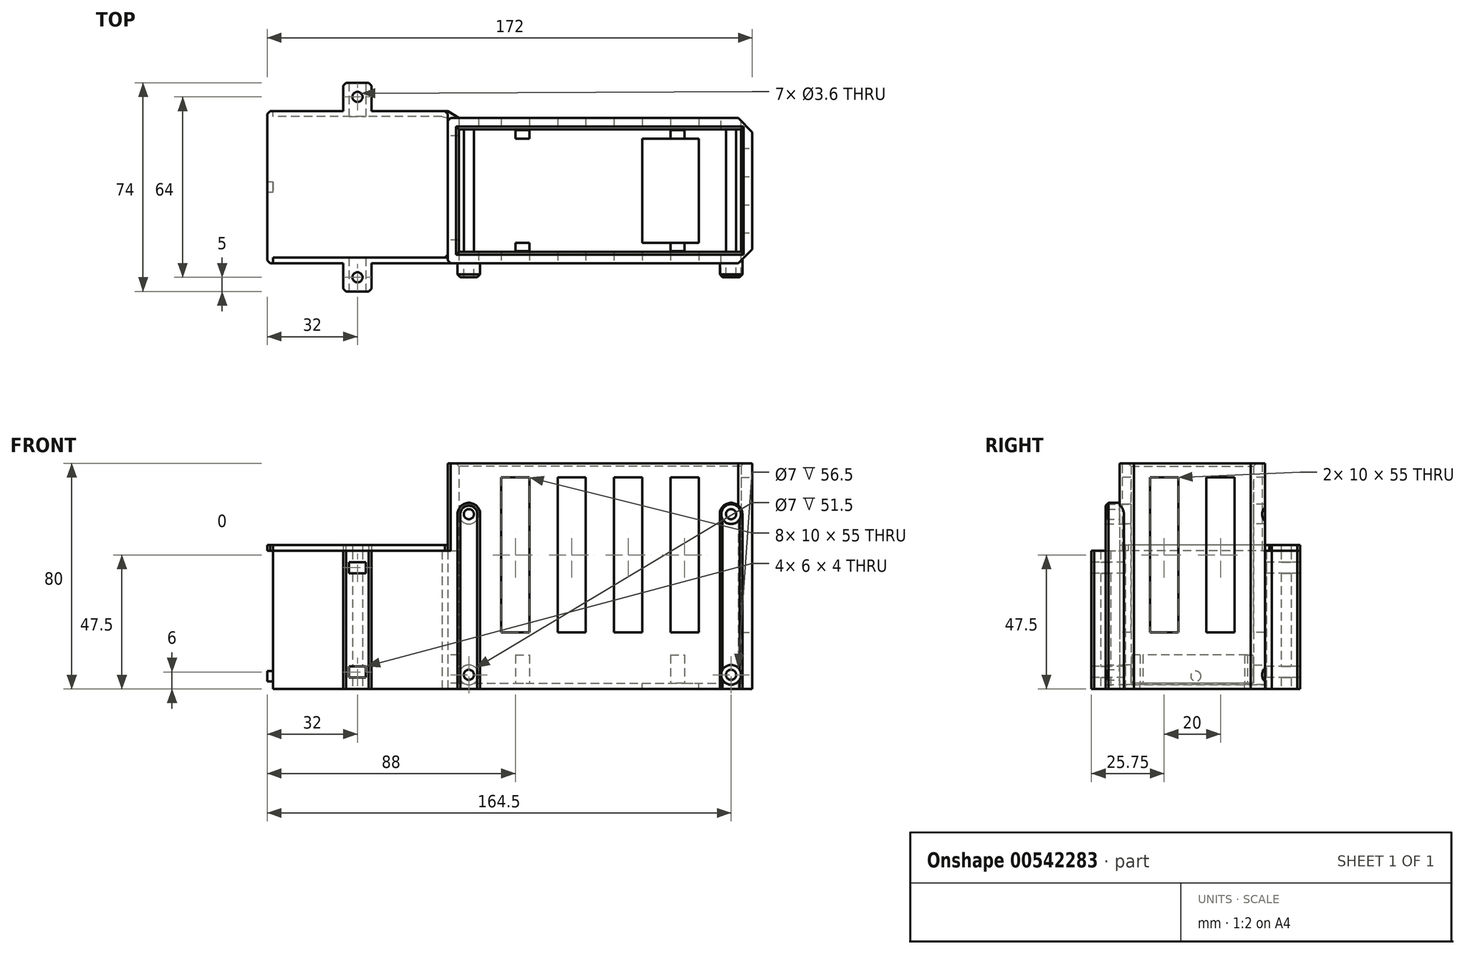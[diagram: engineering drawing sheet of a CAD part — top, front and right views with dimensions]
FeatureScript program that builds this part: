
annotation { "Feature Type Name" : "Feature", "Feature Type Description" : "" }
export const myFeature = defineFeature(function(context is Context, id is Id, definition is map)
    precondition{}
    {
        {
            var Q0;
            Q0=qCreatedBy(makeId("Top.planeOp"),FACE);
            var sketch = newSketch(context, id + "F0", { "sketchPlane" : qUnion([Q0])});
            skLineSegment(sketch, "E0.bottom", {"start": v(-50, 21.75) * mm, "end": v(50, 21.75) * mm});
            skLineSegment(sketch, "E0.top", {"start": v(-50, -21.75) * mm, "end": v(50, -21.75) * mm});
            skLineSegment(sketch, "E0.left", {"start": v(-50, 21.75) * mm, "end": v(-50, -21.75) * mm});
            skLineSegment(sketch, "E0.right", {"start": v(50, 21.75) * mm, "end": v(50, -21.75) * mm});
            skPoint(sketch, "E0.middle", {"position": v(0, 0) * mm});
            skLineSegment(sketch, "E1.0", {"start": v(-54, 25.75) * mm, "end": v(54, 25.75) * mm});
            skLineSegment(sketch, "E1.1", {"start": v(-54, 25.75) * mm, "end": v(-54, -25.75) * mm});
            skLineSegment(sketch, "E1.2", {"start": v(-54, -25.75) * mm, "end": v(54, -25.75) * mm});
            skLineSegment(sketch, "E1.3", {"start": v(54, 25.75) * mm, "end": v(54, -25.75) * mm});
            skLineSegment(sketch, "E2.bottom", {"start": v(-54, -25.75) * mm, "end": v(-118, -25.75) * mm});
            skLineSegment(sketch, "E2.top", {"start": v(-54, 28.25) * mm, "end": v(-118, 28.25) * mm});
            skLineSegment(sketch, "E2.left", {"start": v(-54, -25.75) * mm, "end": v(-54, 25.75) * mm});
            skLineSegment(sketch, "E2.right", {"start": v(-118, -25.75) * mm, "end": v(-118, 28.25) * mm});
            skLineSegment(sketch, "E3.1", {"start": v(-56, -23.75) * mm, "end": v(-116, -23.75) * mm});
            skLineSegment(sketch, "E3.2", {"start": v(-116, -23.75) * mm, "end": v(-116, 26.25) * mm});
            skLineSegment(sketch, "E3.3", {"start": v(-56, 26.25) * mm, "end": v(-116, 26.25) * mm});
            skLineSegment(sketch, "E4", {"start": v(-54, 28.25) * mm, "end": v(-49.99, 25.75) * mm});
            skLineSegment(sketch, "E5", {"start": v(-86, 28.25) * mm, "end": v(-86, 33.25) * mm, "construction": true});
            skLineSegment(sketch, "E6", {"start": v(-116, 1.25) * mm, "end": v(-77.24, 1.25) * mm, "construction": true});
            skLineSegment(sketch, "E7.bottom", {"start": v(-91, 38.25) * mm, "end": v(-81, 38.25) * mm});
            skLineSegment(sketch, "E7.top", {"start": v(-91, 28.25) * mm, "end": v(-81, 28.25) * mm});
            skLineSegment(sketch, "E7.left", {"start": v(-91, 38.25) * mm, "end": v(-91, 28.25) * mm});
            skLineSegment(sketch, "E7.right", {"start": v(-81, 38.25) * mm, "end": v(-81, 28.25) * mm});
            skPoint(sketch, "E7.middle", {"position": v(-86, 33.25) * mm});
            skCircle(sketch, "E8", {"center": v(-86, 33.25) * mm, "radius": 1.8 * mm});
            skLineSegment(sketch, "E9.MirrorCS", {"start": v(-91, -35.75) * mm, "end": v(-91, -25.75) * mm});
            skLineSegment(sketch, "E10.MirrorCS", {"start": v(-91, -35.75) * mm, "end": v(-81, -35.75) * mm});
            skLineSegment(sketch, "E11.MirrorCS", {"start": v(-81, -35.75) * mm, "end": v(-81, -25.75) * mm});
            skCircle(sketch, "E12.MirrorC", {"center": v(-86, -30.75) * mm, "radius": 1.8 * mm});
            skLineSegment(sketch, "E13", {"start": v(-56, 26.25) * mm, "end": v(-54, 25.75) * mm});
            skLineSegment(sketch, "E14", {"start": v(-56, -23.75) * mm, "end": v(-54, -23.75) * mm});
            skSolve(sketch);
        }
        {
            var Q0;
            Q0=makeQuery(id+"F0.imprint","IMPRINT",FACE,{"disambiguationData":[TD([[makeQuery(id+"F0.imprint","IMPRINT",EDGE,{"derivedFrom":sQuery(id+"F0.wireOp",EDGE,"E0.bottom")}),1.0]])]});
            extrude(context, id + "F1", {"entities" : qUnion([Q0]), "depth" : 80 * mm, "offsetDistance" : 25 * mm});
        }
        {
            var Q0;
            Q0=makeQuery(id+"F0.imprint","IMPRINT",FACE,{"disambiguationData":[TD([[makeQuery(id+"F0.imprint","IMPRINT",EDGE,{"derivedFrom":sQuery(id+"F0.wireOp",EDGE,"E0.bottom")}),-1.0]])]});
            extrude(context, id + "F2", {"entities" : qUnion([Q0]), "operationType" : NewBodyOperationType.ADD, "depth" : 2 * mm, "offsetDistance" : 25 * mm});
        }
        {
            var Q0;
            Q0=makeQuery(id+"F1.opExtrude","SWEPT_FACE",FACE,{"disambiguationData":[OSD([sQuery(id+"F0.wireOp",EDGE,"E1.2")])]});
            var sketch = newSketch(context, id + "F3", { "sketchPlane" : qUnion([Q0])});
            skLineSegment(sketch, "E15.bottom", {"start": v(-46.5, 62) * mm, "end": v(46.5, 62) * mm, "construction": true});
            skLineSegment(sketch, "E15.top", {"start": v(-46.5, 5) * mm, "end": v(46.5, 5) * mm, "construction": true});
            skLineSegment(sketch, "E15.left", {"start": v(-46.5, 62) * mm, "end": v(-46.5, 5) * mm, "construction": true});
            skLineSegment(sketch, "E15.right", {"start": v(46.5, 62) * mm, "end": v(46.5, 5) * mm, "construction": true});
            skArc(sketch, "E16", {"start": v(-42.5, 62) * mm, "mid": v(-46.5, 66) * mm, "end": v(-50.5, 62) * mm});
            skLineSegment(sketch, "E17", {"start": v(-50.5, 62) * mm, "end": v(-50.5, 0) * mm});
            skLineSegment(sketch, "E18", {"start": v(-42.5, 62) * mm, "end": v(-42.5, 0) * mm});
            skCircle(sketch, "E19", {"center": v(-46.5, 62) * mm, "radius": 1.8 * mm});
            skCircle(sketch, "E20", {"center": v(-46.5, 5) * mm, "radius": 1.8 * mm});
            skLineSegment(sketch, "E21", {"start": v(0, 0) * mm, "end": v(0, 80) * mm, "construction": true});
            skCircle(sketch, "E22.MirrorC", {"center": v(46.5, 62) * mm, "radius": 1.8 * mm});
            skLineSegment(sketch, "E23.MirrorCS", {"start": v(42.5, 62) * mm, "end": v(42.5, 0) * mm});
            skArc(sketch, "E24.MirrorCS", {"start": v(42.5, 62) * mm, "mid": v(46.5, 66) * mm, "end": v(50.5, 62) * mm});
            skLineSegment(sketch, "E25.MirrorCS", {"start": v(50.5, 62) * mm, "end": v(50.5, 0) * mm});
            skCircle(sketch, "E26.MirrorC", {"center": v(46.5, 5) * mm, "radius": 1.8 * mm});
            skCircle(sketch, "E27", {"center": v(-46.5, 62) * mm, "radius": 3.5 * mm});
            skCircle(sketch, "E28", {"center": v(-46.5, 5) * mm, "radius": 3.5 * mm});
            skCircle(sketch, "E29.MirrorC", {"center": v(46.5, 62) * mm, "radius": 3.5 * mm});
            skCircle(sketch, "E30.MirrorC", {"center": v(46.5, 5) * mm, "radius": 3.5 * mm});
            skSolve(sketch);
        }
        {
            var Q0;
            Q0=makeQuery(id+"F3.imprint","IMPRINT",FACE,{"disambiguationData":[TD([[makeQuery(id+"F3.imprint","IMPRINT",EDGE,{"derivedFrom":sQuery(id+"F3.wireOp",EDGE,"E22.MirrorC")}),1.0]])]});
            var Q1;
            Q1=makeQuery(id+"F3.imprint","IMPRINT",FACE,{"disambiguationData":[TD([[makeQuery(id+"F3.imprint","IMPRINT",EDGE,{"derivedFrom":sQuery(id+"F3.wireOp",EDGE,"E16")}),1.0]])]});
            var Q2;
            Q2=makeQuery(id+"F3.imprint","IMPRINT",FACE,{"disambiguationData":[TD([[makeQuery(id+"F3.imprint","IMPRINT",EDGE,{"derivedFrom":sQuery(id+"F3.wireOp",EDGE,"E19")}),-1.0]])]});
            var Q3;
            Q3=makeQuery(id+"F3.imprint","IMPRINT",FACE,{"disambiguationData":[TD([[makeQuery(id+"F3.imprint","IMPRINT",EDGE,{"derivedFrom":sQuery(id+"F3.wireOp",EDGE,"E20")}),-1.0]])]});
            var Q4;
            {var subQ1=sQuery(id+"F3.wireOp",EDGE,"E23.MirrorCS");Q4=makeQuery(id+"F3.imprint","IMPRINT",FACE,{"disambiguationData":[TD([[makeQuery(id+"F3.imprint","IMPRINT",EDGE,{"derivedFrom":subQ1}),1.0]])]});}
            var Q5;
            Q5=makeQuery(id+"F3.imprint","IMPRINT",FACE,{"disambiguationData":[TD([[makeQuery(id+"F3.imprint","IMPRINT",EDGE,{"derivedFrom":sQuery(id+"F3.wireOp",EDGE,"E26.MirrorC")}),1.0]])]});
            extrude(context, id + "F4", {"entities" : qUnion([Q0, Q1, Q2, Q3, Q4, Q5]), "operationType" : NewBodyOperationType.ADD, "depth" : 5 * mm, "offsetDistance" : 25 * mm});
        }
        {
            var Q0;
            Q0=makeQuery(id+"F3.imprint","IMPRINT",FACE,{"disambiguationData":[TD([[makeQuery(id+"F3.imprint","IMPRINT",EDGE,{"derivedFrom":sQuery(id+"F3.wireOp",EDGE,"E20")}),-1.0]])]});
            var Q1;
            Q1=makeQuery(id+"F3.imprint","IMPRINT",FACE,{"disambiguationData":[TD([[makeQuery(id+"F3.imprint","IMPRINT",EDGE,{"derivedFrom":sQuery(id+"F3.wireOp",EDGE,"E26.MirrorC")}),1.0]])]});
            var Q2;
            Q2=makeQuery(id+"F3.imprint","IMPRINT",FACE,{"disambiguationData":[TD([[makeQuery(id+"F3.imprint","IMPRINT",EDGE,{"derivedFrom":sQuery(id+"F3.wireOp",EDGE,"E22.MirrorC")}),1.0]])]});
            var Q3;
            Q3=makeQuery(id+"F3.imprint","IMPRINT",FACE,{"disambiguationData":[TD([[makeQuery(id+"F3.imprint","IMPRINT",EDGE,{"derivedFrom":sQuery(id+"F3.wireOp",EDGE,"E22.MirrorC")}),-1.0]])]});
            var Q4;
            Q4=makeQuery(id+"F3.imprint","IMPRINT",FACE,{"disambiguationData":[TD([[makeQuery(id+"F3.imprint","IMPRINT",EDGE,{"derivedFrom":sQuery(id+"F3.wireOp",EDGE,"E26.MirrorC")}),-1.0]])]});
            var Q5;
            Q5=makeQuery(id+"F3.imprint","IMPRINT",FACE,{"disambiguationData":[TD([[makeQuery(id+"F3.imprint","IMPRINT",EDGE,{"derivedFrom":sQuery(id+"F3.wireOp",EDGE,"E20")}),1.0]])]});
            var Q6;
            Q6=makeQuery(id+"F3.imprint","IMPRINT",FACE,{"disambiguationData":[TD([[makeQuery(id+"F3.imprint","IMPRINT",EDGE,{"derivedFrom":sQuery(id+"F3.wireOp",EDGE,"E19")}),-1.0]])]});
            var Q7;
            Q7=makeQuery(id+"F3.imprint","IMPRINT",FACE,{"disambiguationData":[TD([[makeQuery(id+"F3.imprint","IMPRINT",EDGE,{"derivedFrom":sQuery(id+"F3.wireOp",EDGE,"E19")}),1.0]])]});
            extrude(context, id + "F5", {"entities" : qUnion([Q0, Q1, Q2, Q3, Q4, Q5, Q6, Q7]), "operationType" : NewBodyOperationType.REMOVE, "oppositeDirection" : true, "depth" : 58 * mm, "offsetDistance" : 25 * mm});
        }
        {
            var Q0;
            {var subQ0=sQuery(id+"F0.wireOp",EDGE,"E0.bottom");var subQ1=makeQuery(id+"F1.opExtrude","SWEPT_FACE",FACE,{"disambiguationData":[OSD([subQ0])]});var subQ2=makeQuery(id+"F5.opExtrude","SWEPT_FACE",FACE,{"disambiguationData":[OSD([sQuery(id+"F3.wireOp",EDGE,"E28")])]});var subQ3=sQuery(id+"F0.wireOp",EDGE,"E0.top");var subQ4=makeQuery(id+"F1.opExtrude","SWEPT_FACE",FACE,{"disambiguationData":[OSD([subQ3])]});var subQ5=makeQuery(id+"F5.opExtrude","SWEPT_FACE",FACE,{"disambiguationData":[OSD([sQuery(id+"F3.wireOp",EDGE,"E30.MirrorC")])]});var subQ6=sQuery(id+"F0.wireOp",EDGE,"E0.right");var subQ7=sQuery(id+"F0.wireOp",EDGE,"E0.left");var subQ8=makeQuery(id+"F2.opExtrude","CAP_FACE",FACE,{"disambiguationData":[OSD([subQ0,subQ3,subQ7,subQ6])],"isStart":false});Q0=qUnion([makeQuery(id+"F5.boolean.opBoolean","SPLIT",FACE,{"disambiguationData":[TD([subQ1,subQ4,makeQuery(id+"F1.opExtrude","SWEPT_FACE",FACE,{"disambiguationData":[OSD([subQ7])]}),subQ2])],"derivedFrom":subQ8}),makeQuery(id+"F5.boolean.opBoolean","SPLIT",FACE,{"disambiguationData":[TD([subQ1,subQ4,makeQuery(id+"F1.opExtrude","SWEPT_FACE",FACE,{"disambiguationData":[OSD([subQ6])]}),subQ5])],"derivedFrom":subQ8}),makeQuery(id+"F5.boolean.opBoolean","SPLIT",FACE,{"disambiguationData":[TD([subQ1,subQ4,subQ2,subQ5])],"derivedFrom":subQ8})]);}
            var sketch = newSketch(context, id + "F6", { "sketchPlane" : qUnion([Q0])});
            skPoint(sketch, "E31.middle", {"position": v(0, 0) * mm});
            skLineSegment(sketch, "E32.bottom", {"start": v(-30, 18.5) * mm, "end": v(30, 18.5) * mm, "construction": true});
            skLineSegment(sketch, "E32.top", {"start": v(-30, -18.5) * mm, "end": v(30, -18.5) * mm, "construction": true});
            skLineSegment(sketch, "E32.left", {"start": v(-30, 18.5) * mm, "end": v(-30, -18.5) * mm, "construction": true});
            skLineSegment(sketch, "E32.right", {"start": v(30, 18.5) * mm, "end": v(30, -18.5) * mm, "construction": true});
            skLineSegment(sketch, "E33.bottom", {"start": v(-30, 18.5) * mm, "end": v(-25, 18.5) * mm});
            skLineSegment(sketch, "E33.top", {"start": v(-30, 21.5) * mm, "end": v(-25, 21.5) * mm});
            skLineSegment(sketch, "E33.left", {"start": v(-30, 18.5) * mm, "end": v(-30, 21.5) * mm});
            skLineSegment(sketch, "E33.right", {"start": v(-25, 18.5) * mm, "end": v(-25, 21.5) * mm});
            skLineSegment(sketch, "E34", {"start": v(0, 0) * mm, "end": v(0, 7.27) * mm, "construction": true});
            skLineSegment(sketch, "E35", {"start": v(0, 0) * mm, "end": v(-7.02, 0) * mm, "construction": true});
            skLineSegment(sketch, "E36.MirrorCS", {"start": v(-25, -18.5) * mm, "end": v(-25, -21.5) * mm});
            skLineSegment(sketch, "E37.MirrorCS", {"start": v(-30, -18.5) * mm, "end": v(-30, -21.5) * mm});
            skLineSegment(sketch, "E38.MirrorCS", {"start": v(-30, -21.5) * mm, "end": v(-25, -21.5) * mm});
            skLineSegment(sketch, "E39.MirrorCS", {"start": v(25, 18.5) * mm, "end": v(25, 21.5) * mm});
            skLineSegment(sketch, "E40.MirrorCS", {"start": v(30, 18.5) * mm, "end": v(30, 21.5) * mm});
            skLineSegment(sketch, "E41.MirrorCS", {"start": v(25, -18.5) * mm, "end": v(25, -21.5) * mm});
            skLineSegment(sketch, "E42.MirrorCS", {"start": v(30, -18.5) * mm, "end": v(30, -21.5) * mm});
            skLineSegment(sketch, "E43.MirrorCS", {"start": v(30, 21.5) * mm, "end": v(25, 21.5) * mm});
            skLineSegment(sketch, "E44.MirrorCS", {"start": v(30, -21.5) * mm, "end": v(25, -21.5) * mm});
            skLineSegment(sketch, "E45", {"start": v(25, 18.5) * mm, "end": v(30, 18.5) * mm});
            skLineSegment(sketch, "E46", {"start": v(-30, -18.5) * mm, "end": v(-25, -18.5) * mm});
            skLineSegment(sketch, "E47", {"start": v(25, -18.5) * mm, "end": v(30, -18.5) * mm});
            skLineSegment(sketch, "E48", {"start": v(0, 0) * mm, "end": v(25, 0) * mm, "construction": true});
            skLineSegment(sketch, "E49.bottom", {"start": v(15, 18.5) * mm, "end": v(35, 18.5) * mm});
            skLineSegment(sketch, "E49.top", {"start": v(15, -18.5) * mm, "end": v(35, -18.5) * mm});
            skLineSegment(sketch, "E49.left", {"start": v(15, 18.5) * mm, "end": v(15, -18.5) * mm});
            skLineSegment(sketch, "E49.right", {"start": v(35, 18.5) * mm, "end": v(35, -18.5) * mm});
            skPoint(sketch, "E49.middle", {"position": v(25, 0) * mm});
            skSolve(sketch);
        }
        {
            var Q0;
            {var subQ4=sQuery(id+"F0.wireOp",EDGE,"E2.right");Q0=makeQuery(id+"F0.imprint","IMPRINT",FACE,{"disambiguationData":[TD([[makeQuery(id+"F0.imprint","IMPRINT",EDGE,{"derivedFrom":subQ4}),-1.0]])]});}
            var Q1;
            Q1=makeQuery(id+"F0.imprint","IMPRINT",FACE,{"disambiguationData":[TD([[makeQuery(id+"F0.imprint","IMPRINT",EDGE,{"derivedFrom":sQuery(id+"F0.wireOp",EDGE,"E7.bottom")}),-1.0]])]});
            var Q2;
            {var subQ0=sQuery(id+"F0.wireOp",EDGE,"E9.MirrorCS");Q2=makeQuery(id+"F0.imprint","IMPRINT",FACE,{"disambiguationData":[TD([[makeQuery(id+"F0.imprint","IMPRINT",EDGE,{"derivedFrom":subQ0}),-1.0]])]});}
            extrude(context, id + "F7", {"entities" : qUnion([Q0, Q1, Q2]), "operationType" : NewBodyOperationType.ADD, "depth" : 49 * mm, "offsetDistance" : 25 * mm});
        }
        {
            var Q0;
            Q0=makeQuery(id+"F7.opExtrude","SWEPT_FACE",FACE,{"disambiguationData":[OSD([sQuery(id+"F0.wireOp",EDGE,"E2.right")])]});
            var sketch = newSketch(context, id + "F8", { "sketchPlane" : qUnion([Q0])});
            skLineSegment(sketch, "E50.bottom", {"start": v(-26.25, 39.5) * mm, "end": v(23.75, 39.5) * mm});
            skLineSegment(sketch, "E50.top", {"start": v(-26.25, 9.5) * mm, "end": v(23.75, 9.5) * mm});
            skLineSegment(sketch, "E50.left", {"start": v(-26.25, 39.5) * mm, "end": v(-26.25, 9.5) * mm});
            skLineSegment(sketch, "E50.right", {"start": v(23.75, 39.5) * mm, "end": v(23.75, 9.5) * mm});
            skPoint(sketch, "E50.middle", {"position": v(-1.25, 24.5) * mm});
            skPoint(sketch, "E50.middle.positionSnap0", {"position": v(25.75, 24.5) * mm});
            skPoint(sketch, "E50.middle.positionSnap1", {"position": v(-1.25, 0) * mm});
            skPoint(sketch, "E50.centerSnap0", {"position": v(25.75, 24.5) * mm});
            skPoint(sketch, "E50.centerSnap1", {"position": v(-1.25, 0) * mm});
            skLineSegment(sketch, "E51", {"start": v(-1.25, 24.5) * mm, "end": v(-1.25, 44.5) * mm, "construction": true});
            skLineSegment(sketch, "E52", {"start": v(-1.25, 24.5) * mm, "end": v(-7.71, 24.5) * mm, "construction": true});
            skCircle(sketch, "E53", {"center": v(-1.25, 44.5) * mm, "radius": 1.8 * mm});
            skCircle(sketch, "E54.MirrorC", {"center": v(-1.25, 4.5) * mm, "radius": 1.8 * mm});
            skSolve(sketch);
        }
        {
            var Q0;
            Q0=makeQuery(id+"F8.imprint","IMPRINT",FACE,{"disambiguationData":[TD([[makeQuery(id+"F8.imprint","IMPRINT",EDGE,{"derivedFrom":sQuery(id+"F8.wireOp",EDGE,"E50.bottom")}),-1.0]])]});
            var Q1;
            Q1=makeQuery(id+"F8.imprint","IMPRINT",FACE,{"disambiguationData":[TD([[makeQuery(id+"F8.imprint","IMPRINT",EDGE,{"derivedFrom":sQuery(id+"F8.wireOp",EDGE,"E54.MirrorC")}),-1.0]])]});
            var Q2;
            Q2=makeQuery(id+"F8.imprint","IMPRINT",FACE,{"disambiguationData":[TD([[makeQuery(id+"F8.imprint","IMPRINT",EDGE,{"derivedFrom":sQuery(id+"F8.wireOp",EDGE,"E53")}),1.0]])]});
            extrude(context, id + "F9", {"entities" : qUnion([Q0, Q1, Q2]), "operationType" : NewBodyOperationType.REMOVE, "oppositeDirection" : true, "depth" : 2 * mm, "offsetDistance" : 25 * mm});
        }
        {
            var Q0;
            Q0=makeQuery(id+"F6.imprint","IMPRINT",FACE,{"disambiguationData":[TD([[makeQuery(id+"F6.imprint","IMPRINT",EDGE,{"derivedFrom":sQuery(id+"F6.wireOp",EDGE,"E33.bottom")}),1.0]])]});
            var Q1;
            {var subQ0=sQuery(id+"F6.wireOp",EDGE,"E36.MirrorCS");Q1=makeQuery(id+"F6.imprint","IMPRINT",FACE,{"disambiguationData":[TD([[makeQuery(id+"F6.imprint","IMPRINT",EDGE,{"derivedFrom":subQ0}),-1.0]])]});}
            var Q2;
            {var subQ0=sQuery(id+"F6.wireOp",EDGE,"E41.MirrorCS");Q2=makeQuery(id+"F6.imprint","IMPRINT",FACE,{"disambiguationData":[TD([[makeQuery(id+"F6.imprint","IMPRINT",EDGE,{"derivedFrom":subQ0}),1.0]])]});}
            var Q3;
            {var subQ0=sQuery(id+"F6.wireOp",EDGE,"E39.MirrorCS");Q3=makeQuery(id+"F6.imprint","IMPRINT",FACE,{"disambiguationData":[TD([[makeQuery(id+"F6.imprint","IMPRINT",EDGE,{"derivedFrom":subQ0}),-1.0]])]});}
            extrude(context, id + "F10", {"entities" : qUnion([Q0, Q1, Q2, Q3]), "operationType" : NewBodyOperationType.ADD, "depth" : 10 * mm, "offsetDistance" : 25 * mm});
        }
        {
            var Q0;
            Q0=makeQuery(id+"F1.opExtrude","SWEPT_FACE",FACE,{"disambiguationData":[OSD([sQuery(id+"F0.wireOp",EDGE,"E1.1")])]});
            var sketch = newSketch(context, id + "F11", { "sketchPlane" : qUnion([Q0])});
            skLineSegment(sketch, "E55", {"start": v(-1, 0) * mm, "end": v(-1, 7) * mm, "construction": true});
            skLineSegment(sketch, "E56.bottom", {"start": v(-19.5, 12) * mm, "end": v(17.5, 12) * mm});
            skLineSegment(sketch, "E56.top", {"start": v(-19.5, 2) * mm, "end": v(17.5, 2) * mm});
            skLineSegment(sketch, "E56.left", {"start": v(-19.5, 12) * mm, "end": v(-19.5, 2) * mm});
            skLineSegment(sketch, "E56.right", {"start": v(17.5, 12) * mm, "end": v(17.5, 2) * mm});
            skPoint(sketch, "E56.middle", {"position": v(-1, 7) * mm});
            skSolve(sketch);
        }
        {
            var Q0;
            Q0=makeQuery(id+"F11.imprint","IMPRINT",FACE,{"disambiguationData":[TD([[makeQuery(id+"F11.imprint","IMPRINT",EDGE,{"derivedFrom":sQuery(id+"F11.wireOp",EDGE,"E56.bottom")}),-1.0]])]});
            extrude(context, id + "F12", {"entities" : qUnion([Q0]), "operationType" : NewBodyOperationType.REMOVE, "oppositeDirection" : true, "depth" : 4 * mm, "offsetDistance" : 25 * mm});
        }
        {
            var Q0;
            Q0=makeQuery(id+"F7.opExtrude","CAP_FACE",FACE,{"disambiguationData":[OSD([sQuery(id+"F0.wireOp",EDGE,"E1.0"),sQuery(id+"F0.wireOp",EDGE,"E1.1"),sQuery(id+"F0.wireOp",EDGE,"E2.bottom"),sQuery(id+"F0.wireOp",EDGE,"E2.top"),sQuery(id+"F0.wireOp",EDGE,"E2.right"),sQuery(id+"F0.wireOp",EDGE,"E3.1"),sQuery(id+"F0.wireOp",EDGE,"E3.2"),sQuery(id+"F0.wireOp",EDGE,"E3.3"),sQuery(id+"F0.wireOp",EDGE,"E4"),sQuery(id+"F0.wireOp",EDGE,"E7.bottom"),sQuery(id+"F0.wireOp",EDGE,"E7.left"),sQuery(id+"F0.wireOp",EDGE,"E7.right"),sQuery(id+"F0.wireOp",EDGE,"E8"),sQuery(id+"F0.wireOp",EDGE,"E9.MirrorCS"),sQuery(id+"F0.wireOp",EDGE,"E10.MirrorCS"),sQuery(id+"F0.wireOp",EDGE,"E11.MirrorCS"),sQuery(id+"F0.wireOp",EDGE,"E12.MirrorC"),sQuery(id+"F0.wireOp",EDGE,"E13"),sQuery(id+"F0.wireOp",EDGE,"E14")])],"isStart":false});
            var sketch = newSketch(context, id + "F13", { "sketchPlane" : qUnion([Q0])});
            skLineSegment(sketch, "E57.right", {"start": v(-54, 26.25) * mm, "end": v(-54, -23.75) * mm});
            skLineSegment(sketch, "E58", {"start": v(-54, 26.25) * mm, "end": v(-54, 28.25) * mm});
            skLineSegment(sketch, "E59", {"start": v(-54, 28.25) * mm, "end": v(-81, 28.25) * mm});
            skLineSegment(sketch, "E60", {"start": v(-81, 28.25) * mm, "end": v(-81, 38.25) * mm});
            skLineSegment(sketch, "E61", {"start": v(-81, 38.25) * mm, "end": v(-91, 38.25) * mm});
            skLineSegment(sketch, "E62", {"start": v(-91, 38.25) * mm, "end": v(-91, 28.25) * mm});
            skLineSegment(sketch, "E63", {"start": v(-91, 28.25) * mm, "end": v(-118, 28.25) * mm});
            skLineSegment(sketch, "E64", {"start": v(-118, 28.25) * mm, "end": v(-118, -25.75) * mm});
            skLineSegment(sketch, "E65", {"start": v(-118, -25.75) * mm, "end": v(-91, -25.75) * mm});
            skLineSegment(sketch, "E66", {"start": v(-91, -25.75) * mm, "end": v(-91, -35.75) * mm});
            skLineSegment(sketch, "E67", {"start": v(-91, -35.75) * mm, "end": v(-81, -35.75) * mm});
            skLineSegment(sketch, "E68", {"start": v(-81, -35.75) * mm, "end": v(-81, -25.75) * mm});
            skLineSegment(sketch, "E69", {"start": v(-81, -25.75) * mm, "end": v(-54, -25.75) * mm});
            skLineSegment(sketch, "E70", {"start": v(-54, -25.75) * mm, "end": v(-54, -23.75) * mm});
            skCircle(sketch, "E71", {"center": v(-86, 33.25) * mm, "radius": 1.8 * mm});
            skCircle(sketch, "E72", {"center": v(-86, -30.75) * mm, "radius": 1.8 * mm});
            skSolve(sketch);
        }
        {
            var Q0;
            {var subQ2=sQuery(id+"F13.wireOp",EDGE,"E58");Q0=makeQuery(id+"F13.imprint","IMPRINT",FACE,{"disambiguationData":[TD([[makeQuery(id+"F13.imprint","IMPRINT",EDGE,{"derivedFrom":subQ2}),1.0]])]});}
            var Q1;
            Q1=makeQuery(id+"F13.imprint","IMPRINT",FACE,{"disambiguationData":[TD([[makeQuery(id+"F13.imprint","IMPRINT",EDGE,{"derivedFrom":makeQuery(id+"F7.opExtrude","CAP_EDGE",EDGE,{"disambiguationData":[OSD([sQuery(id+"F0.wireOp",EDGE,"E3.2")])],"isStart":false})}),-1.0]])]});
            extrude(context, id + "F14", {"entities" : qUnion([Q0, Q1]), "depth" : 2 * mm, "offsetDistance" : 25 * mm});
        }
        {
            var Q0;
            {var subQ2=sQuery(id+"F6.wireOp",EDGE,"E49.left");Q0=makeQuery(id+"F6.imprint","IMPRINT",FACE,{"disambiguationData":[TD([[makeQuery(id+"F6.imprint","IMPRINT",EDGE,{"derivedFrom":subQ2}),1.0]])]});}
            extrude(context, id + "F15", {"entities" : qUnion([Q0]), "operationType" : NewBodyOperationType.REMOVE, "oppositeDirection" : true, "depth" : 4 * mm, "offsetDistance" : 25 * mm});
        }
        {
            var Q0;
            {var subQ0=sQuery(id+"F0.wireOp",EDGE,"E2.bottom");var subQ1=sQuery(id+"F0.wireOp",EDGE,"E1.2");var subQ2=sQuery(id+"F0.wireOp",EDGE,"E1.1");Q0=makeQuery(id+"F7.boolean.opBoolean","MERGE",FACE,{"derivedFrom":[makeQuery(id+"F4.boolean.opBoolean","SPLIT",FACE,{"disambiguationData":[TD([makeQuery(id+"F1.opExtrude","SWEPT_FACE",FACE,{"disambiguationData":[OSD([subQ2])]})])],"derivedFrom":makeQuery(id+"F1.opExtrude","SWEPT_FACE",FACE,{"disambiguationData":[OSD([subQ1])]})}),makeQuery(id+"F7.opExtrude","SWEPT_FACE",FACE,{"disambiguationData":[OSD([subQ0]),TDD([makeQuery(id+"F0.imprint","IMPRINT",EDGE,{"disambiguationData":[TD([[makeQuery(id+"F0.imprint","INTERSECT",VERTEX,{"derivedFrom":[subQ0,sQuery(id+"F0.wireOp",EDGE,"E11.MirrorCS")]}),1.0]])],"derivedFrom":subQ0})])]})]});}
            var sketch = newSketch(context, id + "F16", { "sketchPlane" : qUnion([Q0])});
            skLineSegment(sketch, "E73", {"start": v(0, 0) * mm, "end": v(0, 20) * mm, "construction": true});
            skLineSegment(sketch, "E74", {"start": v(0, 20) * mm, "end": v(-35, 20) * mm, "construction": true});
            skLineSegment(sketch, "E75.bottom", {"start": v(-35, 20) * mm, "end": v(35, 20) * mm});
            skLineSegment(sketch, "E75.top", {"start": v(-35, 75) * mm, "end": v(35, 75) * mm});
            skLineSegment(sketch, "E75.left", {"start": v(-35, 20) * mm, "end": v(-35, 75) * mm});
            skLineSegment(sketch, "E75.right", {"start": v(35, 20) * mm, "end": v(35, 75) * mm});
            skLineSegment(sketch, "E76", {"start": v(-35, 75) * mm, "end": v(-25, 75) * mm, "construction": true});
            skLineSegment(sketch, "E77", {"start": v(-25, 75) * mm, "end": v(-15, 75) * mm, "construction": true});
            skLineSegment(sketch, "E78", {"start": v(-15, 75) * mm, "end": v(-5, 75) * mm, "construction": true});
            skLineSegment(sketch, "E79", {"start": v(-5, 75) * mm, "end": v(5, 75) * mm, "construction": true});
            skLineSegment(sketch, "E80", {"start": v(5, 75) * mm, "end": v(15, 75) * mm, "construction": true});
            skLineSegment(sketch, "E81", {"start": v(15, 75) * mm, "end": v(25, 75) * mm, "construction": true});
            skLineSegment(sketch, "E82", {"start": v(25, 75) * mm, "end": v(35, 75) * mm, "construction": true});
            skLineSegment(sketch, "E83", {"start": v(-25, 75) * mm, "end": v(-25, 20) * mm});
            skLineSegment(sketch, "E84", {"start": v(-15, 75) * mm, "end": v(-15, 20) * mm});
            skLineSegment(sketch, "E85", {"start": v(-5, 75) * mm, "end": v(-5, 20) * mm});
            skLineSegment(sketch, "E86", {"start": v(5, 75) * mm, "end": v(5, 20) * mm});
            skLineSegment(sketch, "E87", {"start": v(15, 75) * mm, "end": v(15, 20) * mm});
            skLineSegment(sketch, "E88", {"start": v(25, 75) * mm, "end": v(25, 20) * mm});
            skSolve(sketch);
        }
        {
            var Q0;
            {var subQ0=sQuery(id+"F16.wireOp",EDGE,"E75.left");Q0=makeQuery(id+"F16.imprint","IMPRINT",FACE,{"disambiguationData":[TD([[makeQuery(id+"F16.imprint","IMPRINT",EDGE,{"derivedFrom":subQ0}),-1.0]])]});}
            var Q1;
            {var subQ0=sQuery(id+"F16.wireOp",EDGE,"E84");Q1=makeQuery(id+"F16.imprint","IMPRINT",FACE,{"disambiguationData":[TD([[makeQuery(id+"F16.imprint","IMPRINT",EDGE,{"derivedFrom":subQ0}),1.0]])]});}
            var Q2;
            {var subQ0=sQuery(id+"F16.wireOp",EDGE,"E86");Q2=makeQuery(id+"F16.imprint","IMPRINT",FACE,{"disambiguationData":[TD([[makeQuery(id+"F16.imprint","IMPRINT",EDGE,{"derivedFrom":subQ0}),1.0]])]});}
            var Q3;
            {var subQ0=sQuery(id+"F16.wireOp",EDGE,"E75.right");Q3=makeQuery(id+"F16.imprint","IMPRINT",FACE,{"disambiguationData":[TD([[makeQuery(id+"F16.imprint","IMPRINT",EDGE,{"derivedFrom":subQ0}),1.0]])]});}
            extrude(context, id + "F17", {"entities" : qUnion([Q0, Q1, Q2, Q3]), "operationType" : NewBodyOperationType.REMOVE, "oppositeDirection" : true, "depth" : 51.5 * mm, "offsetDistance" : 25 * mm});
        }
        {
            var Q0;
            Q0=makeQuery(id+"F1.opExtrude","SWEPT_FACE",FACE,{"disambiguationData":[OSD([sQuery(id+"F0.wireOp",EDGE,"E1.3")])]});
            var sketch = newSketch(context, id + "F18", { "sketchPlane" : qUnion([Q0])});
            skLineSegment(sketch, "E89", {"start": v(0, 0) * mm, "end": v(0, 20) * mm, "construction": true});
            skLineSegment(sketch, "E90", {"start": v(0, 20) * mm, "end": v(-15, 20) * mm, "construction": true});
            skLineSegment(sketch, "E91.bottom", {"start": v(-15, 20) * mm, "end": v(15, 20) * mm});
            skLineSegment(sketch, "E91.top", {"start": v(-15, 75) * mm, "end": v(15, 75) * mm});
            skLineSegment(sketch, "E91.left", {"start": v(-15, 20) * mm, "end": v(-15, 75) * mm});
            skLineSegment(sketch, "E91.right", {"start": v(15, 20) * mm, "end": v(15, 75) * mm});
            skLineSegment(sketch, "E92", {"start": v(-15, 75) * mm, "end": v(-5, 75) * mm, "construction": true});
            skLineSegment(sketch, "E93", {"start": v(-5, 75) * mm, "end": v(5, 75) * mm, "construction": true});
            skLineSegment(sketch, "E94", {"start": v(5, 75) * mm, "end": v(15, 75) * mm, "construction": true});
            skLineSegment(sketch, "E95", {"start": v(-5, 75) * mm, "end": v(-5, 20) * mm});
            skLineSegment(sketch, "E96", {"start": v(5, 75) * mm, "end": v(5, 20) * mm});
            skSolve(sketch);
        }
        {
            var Q0;
            {var subQ0=sQuery(id+"F18.wireOp",EDGE,"E91.left");Q0=makeQuery(id+"F18.imprint","IMPRINT",FACE,{"disambiguationData":[TD([[makeQuery(id+"F18.imprint","IMPRINT",EDGE,{"derivedFrom":subQ0}),-1.0]])]});}
            var Q1;
            {var subQ0=sQuery(id+"F18.wireOp",EDGE,"E91.right");Q1=makeQuery(id+"F18.imprint","IMPRINT",FACE,{"disambiguationData":[TD([[makeQuery(id+"F18.imprint","IMPRINT",EDGE,{"derivedFrom":subQ0}),1.0]])]});}
            extrude(context, id + "F19", {"entities" : qUnion([Q0, Q1]), "operationType" : NewBodyOperationType.REMOVE, "oppositeDirection" : true, "depth" : 4 * mm, "offsetDistance" : 25 * mm});
        }
        {
            var Q0;
            Q0=makeQuery(id+"F7.opExtrude","SWEPT_FACE",FACE,{"disambiguationData":[OSD([sQuery(id+"F0.wireOp",EDGE,"E10.MirrorCS")])]});
            var sketch = newSketch(context, id + "F20", { "sketchPlane" : qUnion([Q0])});
            skLineSegment(sketch, "E97", {"start": v(-86, 49) * mm, "end": v(-86, 43) * mm, "construction": true});
            skLineSegment(sketch, "E98.bottom", {"start": v(-89, 45) * mm, "end": v(-83, 45) * mm});
            skLineSegment(sketch, "E98.top", {"start": v(-89, 41) * mm, "end": v(-83, 41) * mm});
            skLineSegment(sketch, "E98.left", {"start": v(-89, 45) * mm, "end": v(-89, 41) * mm});
            skLineSegment(sketch, "E98.right", {"start": v(-83, 45) * mm, "end": v(-83, 41) * mm});
            skPoint(sketch, "E98.middle", {"position": v(-86, 43) * mm});
            skLineSegment(sketch, "E99", {"start": v(-81, 24.5) * mm, "end": v(-91, 24.5) * mm, "construction": true});
            skLineSegment(sketch, "E100.MirrorCS", {"start": v(-89, 8) * mm, "end": v(-83, 8) * mm});
            skLineSegment(sketch, "E101.MirrorCS", {"start": v(-83, 4) * mm, "end": v(-83, 8) * mm});
            skLineSegment(sketch, "E102.MirrorCS", {"start": v(-89, 4) * mm, "end": v(-83, 4) * mm});
            skLineSegment(sketch, "E103.MirrorCS", {"start": v(-89, 4) * mm, "end": v(-89, 8) * mm});
            skSolve(sketch);
        }
        {
            var Q0;
            Q0=makeQuery(id+"F20.imprint","IMPRINT",FACE,{"disambiguationData":[TD([[makeQuery(id+"F20.imprint","IMPRINT",EDGE,{"derivedFrom":sQuery(id+"F20.wireOp",EDGE,"E98.bottom")}),-1.0]])]});
            var Q1;
            Q1=makeQuery(id+"F20.imprint","IMPRINT",FACE,{"disambiguationData":[TD([[makeQuery(id+"F20.imprint","IMPRINT",EDGE,{"derivedFrom":sQuery(id+"F20.wireOp",EDGE,"E100.MirrorCS")}),-1.0]])]});
            extrude(context, id + "F21", {"entities" : qUnion([Q0, Q1]), "operationType" : NewBodyOperationType.REMOVE, "oppositeDirection" : true, "depth" : 74 * mm, "offsetDistance" : 25 * mm});
        }
        {
            var Q0;
            Q0=makeQuery(id+"F1.opExtrude","SWEPT_EDGE",EDGE,{"disambiguationData":[OSD([sQuery(id+"F0.wireOp",EDGE,"E1.2"),sQuery(id+"F0.wireOp",EDGE,"E1.3")])]});
            var Q1;
            Q1=makeQuery(id+"F1.opExtrude","SWEPT_EDGE",EDGE,{"disambiguationData":[OSD([sQuery(id+"F0.wireOp",EDGE,"E1.0"),sQuery(id+"F0.wireOp",EDGE,"E1.3")])]});
            chamfer(context, id + "F22", {"entities" : qUnion([Q0, Q1]), "width" : 5 * mm, "tangentPropagation" : true});
        }
        {
            var Q0;
            Q0=makeQuery(id+"F1.opExtrude","CAP_EDGE",EDGE,{"disambiguationData":[OSD([sQuery(id+"F0.wireOp",EDGE,"E0.bottom")])],"isStart":false});
            var Q1;
            Q1=makeQuery(id+"F1.opExtrude","CAP_EDGE",EDGE,{"disambiguationData":[OSD([sQuery(id+"F0.wireOp",EDGE,"E0.left")])],"isStart":false});
            var Q2;
            Q2=makeQuery(id+"F1.opExtrude","CAP_EDGE",EDGE,{"disambiguationData":[OSD([sQuery(id+"F0.wireOp",EDGE,"E0.top")])],"isStart":false});
            var Q3;
            Q3=makeQuery(id+"F1.opExtrude","CAP_EDGE",EDGE,{"disambiguationData":[OSD([sQuery(id+"F0.wireOp",EDGE,"E0.right")])],"isStart":false});
            var Q4;
            Q4=makeQuery(id+"F4.opExtrude","CAP_EDGE",EDGE,{"disambiguationData":[OSD([sQuery(id+"F3.wireOp",EDGE,"E18")])],"isStart":false});
            var Q5;
            Q5=makeQuery(id+"F4.opExtrude","CAP_EDGE",EDGE,{"disambiguationData":[OSD([sQuery(id+"F3.wireOp",EDGE,"E17")])],"isStart":false});
            var Q6;
            Q6=makeQuery(id+"F4.opExtrude","CAP_EDGE",EDGE,{"disambiguationData":[OSD([sQuery(id+"F3.wireOp",EDGE,"E23.MirrorCS")])],"isStart":false});
            var Q7;
            Q7=makeQuery(id+"F7.opExtrude","SWEPT_EDGE",EDGE,{"disambiguationData":[OSD([sQuery(id+"F0.wireOp",EDGE,"E2.bottom"),sQuery(id+"F0.wireOp",EDGE,"E2.right")])]});
            var Q8;
            Q8=makeQuery(id+"F14.opExtrude","SWEPT_EDGE",EDGE,{"disambiguationData":[OSD([sQuery(id+"F13.wireOp",EDGE,"E64"),sQuery(id+"F13.wireOp",EDGE,"E65")])]});
            var Q9;
            Q9=makeQuery(id+"F7.opExtrude","SWEPT_EDGE",EDGE,{"disambiguationData":[OSD([sQuery(id+"F0.wireOp",EDGE,"E2.top"),sQuery(id+"F0.wireOp",EDGE,"E2.right")])]});
            var Q10;
            Q10=makeQuery(id+"F14.opExtrude","SWEPT_EDGE",EDGE,{"disambiguationData":[OSD([sQuery(id+"F13.wireOp",EDGE,"E63"),sQuery(id+"F13.wireOp",EDGE,"E64")])]});
            var Q11;
            Q11=makeQuery(id+"F14.opExtrude","SWEPT_EDGE",EDGE,{"disambiguationData":[OSD([sQuery(id+"F0.wireOp",EDGE,"E4"),sQuery(id+"F13.wireOp",EDGE,"E58"),sQuery(id+"F13.wireOp",EDGE,"E59")])]});
            var Q12;
            Q12=makeQuery(id+"F14.opExtrude","SWEPT_EDGE",EDGE,{"disambiguationData":[OSD([sQuery(id+"F13.wireOp",EDGE,"E69"),sQuery(id+"F13.wireOp",EDGE,"E70")])]});
            var Q13;
            Q13=makeQuery(id+"F1.opExtrude","SWEPT_EDGE",EDGE,{"disambiguationData":[OSD([sQuery(id+"F0.wireOp",EDGE,"E1.1"),sQuery(id+"F0.wireOp",EDGE,"E1.2"),sQuery(id+"F0.wireOp",EDGE,"E2.bottom")])]});
            var Q14;
            Q14=makeQuery(id+"F7.boolean.opBoolean","SPLIT",EDGE,{"derivedFrom":makeQuery(id+"F1.opExtrude","SWEPT_EDGE",EDGE,{"disambiguationData":[OSD([sQuery(id+"F0.wireOp",EDGE,"E1.0"),sQuery(id+"F0.wireOp",EDGE,"E1.1"),sQuery(id+"F0.wireOp",EDGE,"E13")])]})});
            var Q15;
            Q15=makeQuery(id+"F7.opExtrude","SWEPT_EDGE",EDGE,{"disambiguationData":[OSD([sQuery(id+"F0.wireOp",EDGE,"E10.MirrorCS"),sQuery(id+"F0.wireOp",EDGE,"E11.MirrorCS")])]});
            var Q16;
            Q16=makeQuery(id+"F7.opExtrude","SWEPT_EDGE",EDGE,{"disambiguationData":[OSD([sQuery(id+"F0.wireOp",EDGE,"E9.MirrorCS"),sQuery(id+"F0.wireOp",EDGE,"E10.MirrorCS")])]});
            var Q17;
            Q17=makeQuery(id+"F14.opExtrude","SWEPT_EDGE",EDGE,{"disambiguationData":[OSD([sQuery(id+"F13.wireOp",EDGE,"E66"),sQuery(id+"F13.wireOp",EDGE,"E67")])]});
            var Q18;
            Q18=makeQuery(id+"F14.opExtrude","SWEPT_EDGE",EDGE,{"disambiguationData":[OSD([sQuery(id+"F13.wireOp",EDGE,"E67"),sQuery(id+"F13.wireOp",EDGE,"E68")])]});
            var Q19;
            Q19=makeQuery(id+"F14.opExtrude","SWEPT_EDGE",EDGE,{"disambiguationData":[OSD([sQuery(id+"F13.wireOp",EDGE,"E60"),sQuery(id+"F13.wireOp",EDGE,"E61")])]});
            var Q20;
            Q20=makeQuery(id+"F14.opExtrude","SWEPT_EDGE",EDGE,{"disambiguationData":[OSD([sQuery(id+"F13.wireOp",EDGE,"E61"),sQuery(id+"F13.wireOp",EDGE,"E62")])]});
            var Q21;
            Q21=makeQuery(id+"F7.opExtrude","SWEPT_EDGE",EDGE,{"disambiguationData":[OSD([sQuery(id+"F0.wireOp",EDGE,"E7.bottom"),sQuery(id+"F0.wireOp",EDGE,"E7.right")])]});
            var Q22;
            Q22=makeQuery(id+"F7.opExtrude","SWEPT_EDGE",EDGE,{"disambiguationData":[OSD([sQuery(id+"F0.wireOp",EDGE,"E7.bottom"),sQuery(id+"F0.wireOp",EDGE,"E7.left")])]});
            chamfer(context, id + "F23", {"entities" : qUnion([Q0, Q1, Q2, Q3, Q4, Q5, Q6, Q7, Q8, Q9, Q10, Q11, Q12, Q13, Q14, Q15, Q16, Q17, Q18, Q19, Q20, Q21, Q22]), "width" : 1 * mm, "tangentPropagation" : true});
        }
    });
